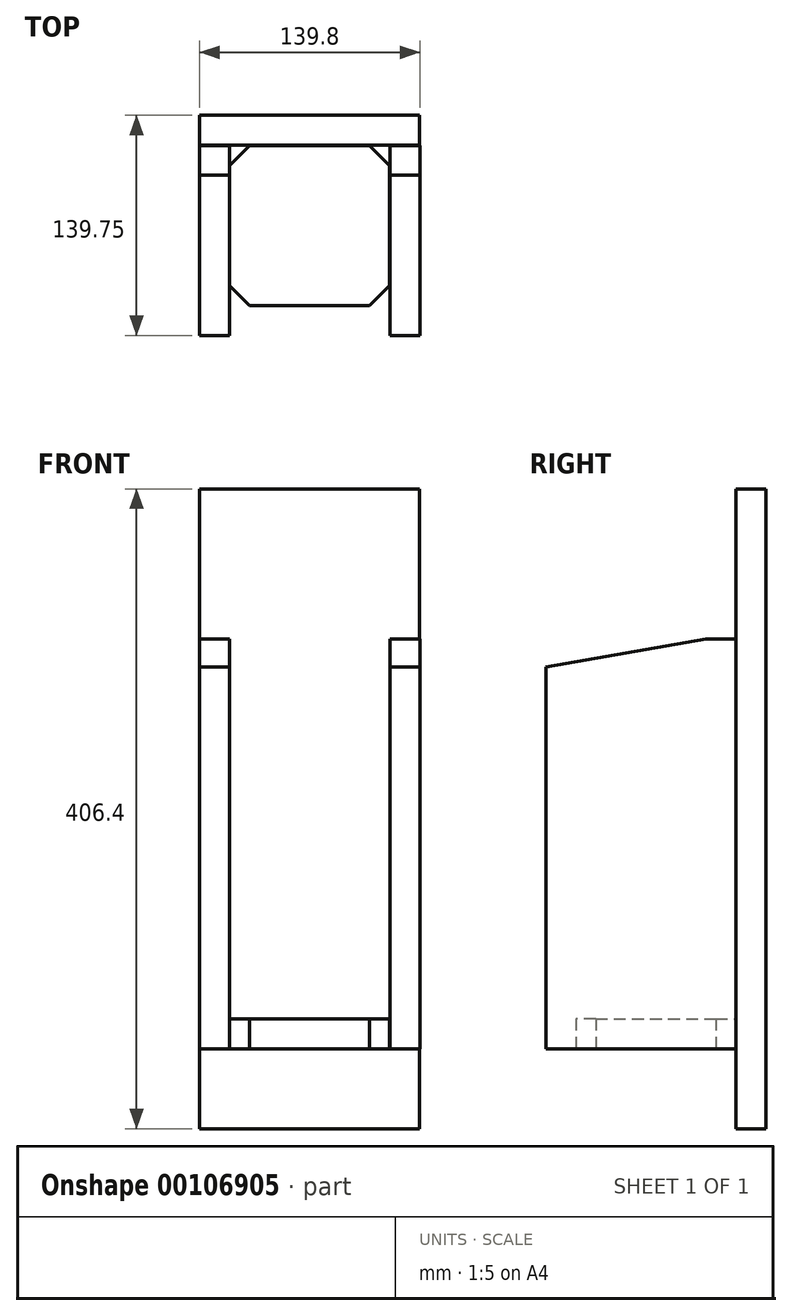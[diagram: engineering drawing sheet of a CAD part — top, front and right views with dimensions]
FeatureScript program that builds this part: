
annotation { "Feature Type Name" : "Feature", "Feature Type Description" : "" }
export const myFeature = defineFeature(function(context is Context, id is Id, definition is map)
    precondition{}
    {
        {
            var Q0;
            Q0=qCreatedBy(makeId("Top.planeOp"),FACE);
            var sketch = newSketch(context, id + "F0", { "sketchPlane" : qUnion([Q0])});
            skLineSegment(sketch, "E0.bottom", {"start": v(38.1, -50.8) * mm, "end": v(-38.1, -50.8) * mm});
            skLineSegment(sketch, "E0.top", {"start": v(38.1, 50.8) * mm, "end": v(-38.1, 50.8) * mm});
            skLineSegment(sketch, "E0.left", {"start": v(50.8, -38.1) * mm, "end": v(50.8, 38.1) * mm});
            skLineSegment(sketch, "E0.right", {"start": v(-50.8, -38.1) * mm, "end": v(-50.8, 38.1) * mm});
            skPoint(sketch, "E0.middle", {"position": v(0, 0) * mm});
            skLineSegment(sketch, "E1", {"start": v(-50.8, 38.1) * mm, "end": v(-38.1, 50.8) * mm});
            skPoint(sketch, "E2.orphan", {"position": v(-50.8, 50.8) * mm});
            skLineSegment(sketch, "E3", {"start": v(38.1, 50.8) * mm, "end": v(50.8, 38.1) * mm});
            skLineSegment(sketch, "E4", {"start": v(-50.8, -38.1) * mm, "end": v(-38.1, -50.8) * mm});
            skLineSegment(sketch, "E5", {"start": v(38.1, -50.8) * mm, "end": v(50.8, -38.1) * mm});
            skPoint(sketch, "E6.orphan", {"position": v(50.8, 50.8) * mm});
            skPoint(sketch, "E7.orphan", {"position": v(50.8, -50.8) * mm});
            skPoint(sketch, "E8.orphan", {"position": v(-50.8, -50.8) * mm});
            skSolve(sketch);
        }
        {
            var Q0;
            Q0=makeQuery(id+"F0.imprint","IMPRINT",FACE,{"disambiguationData":[TD([[makeQuery(id+"F0.imprint","IMPRINT",EDGE,{"derivedFrom":sQuery(id+"F0.wireOp",EDGE,"E0.bottom")}),-1.0]])]});
            extrude(context, id + "F1", {"entities" : qUnion([Q0]), "depth" : 19.05 * mm});
        }
        {
            var Q0;
            Q0=qCreatedBy(makeId("Top.planeOp"),FACE);
            var sketch = newSketch(context, id + "F2", { "sketchPlane" : qUnion([Q0])});
            skLineSegment(sketch, "E9.bottom", {"start": v(-69.85, 50.85) * mm, "end": v(69.85, 50.85) * mm});
            skLineSegment(sketch, "E9.top", {"start": v(-69.85, 69.9) * mm, "end": v(69.85, 69.9) * mm});
            skLineSegment(sketch, "E9.left", {"start": v(-69.85, 50.85) * mm, "end": v(-69.85, 69.9) * mm});
            skLineSegment(sketch, "E9.right", {"start": v(69.85, 50.85) * mm, "end": v(69.85, 69.9) * mm});
            skSolve(sketch);
        }
        {
            var Q0;
            Q0=makeQuery(id+"F2.imprint","IMPRINT",FACE,{"disambiguationData":[TD([[makeQuery(id+"F2.imprint","IMPRINT",EDGE,{"derivedFrom":sQuery(id+"F2.wireOp",EDGE,"E9.bottom")}),1.0]])]});
            extrude(context, id + "F3", {"entities" : qUnion([Q0]), "depth" : 355.6 * mm, "hasSecondDirection" : true, "secondDirectionOppositeDirection" : true, "secondDirectionDepth" : 50.8 * mm});
        }
        {
            var Q0;
            Q0=qCreatedBy(makeId("Top.planeOp"),FACE);
            var sketch = newSketch(context, id + "F4", { "sketchPlane" : qUnion([Q0])});
            skLineSegment(sketch, "E10.bottom", {"start": v(50.85, 50.8) * mm, "end": v(69.9, 50.8) * mm});
            skLineSegment(sketch, "E10.top", {"start": v(50.85, -69.85) * mm, "end": v(69.9, -69.85) * mm});
            skLineSegment(sketch, "E10.left", {"start": v(50.85, 50.8) * mm, "end": v(50.85, -69.85) * mm});
            skLineSegment(sketch, "E10.right", {"start": v(69.9, 50.8) * mm, "end": v(69.9, -69.85) * mm});
            skSolve(sketch);
        }
        {
            var Q0;
            Q0=makeQuery(id+"F4.imprint","IMPRINT",FACE,{"disambiguationData":[TD([[makeQuery(id+"F4.imprint","IMPRINT",EDGE,{"derivedFrom":sQuery(id+"F4.wireOp",EDGE,"E10.bottom")}),-1.0]])]});
            extrude(context, id + "F5", {"entities" : qUnion([Q0]), "depth" : 260.35 * mm});
        }
        {
            var Q0;
            Q0=makeQuery(id+"F5.opExtrude","SWEPT_FACE",FACE,{"disambiguationData":[OSD([sQuery(id+"F4.wireOp",EDGE,"E10.right")])]});
            var sketch = newSketch(context, id + "F6", { "sketchPlane" : qUnion([Q0])});
            skLineSegment(sketch, "E11", {"start": v(-69.85, 260.35) * mm, "end": v(-69.85, 242.43) * mm});
            skLineSegment(sketch, "E12", {"start": v(-69.85, 242.43) * mm, "end": v(31.8, 260.35) * mm});
            skLineSegment(sketch, "E13", {"start": v(31.8, 260.35) * mm, "end": v(-69.85, 260.35) * mm});
            skSolve(sketch);
        }
        {
            var Q0;
            Q0=makeQuery(id+"F6.imprint","IMPRINT",FACE,{"disambiguationData":[TD([[makeQuery(id+"F6.imprint","IMPRINT",EDGE,{"derivedFrom":sQuery(id+"F6.wireOp",EDGE,"E11")}),1.0]])]});
            extrude(context, id + "F7", {"entities" : qUnion([Q0]), "operationType" : NewBodyOperationType.REMOVE, "endBound" : BoundingType.THROUGH_ALL, "oppositeDirection" : true, "depth" : 25.4 * mm});
        }
        {
            var Q0;
            Q0=makeQuery(id+"F5.opExtrude","SWEPT_BODY",BODY,{"disambiguationData":[OSD([sQuery(id+"F4.wireOp",EDGE,"E10.bottom"),sQuery(id+"F4.wireOp",EDGE,"E10.top"),sQuery(id+"F4.wireOp",EDGE,"E10.left"),sQuery(id+"F4.wireOp",EDGE,"E10.right")])]});
            var Q1;
            Q1=qCreatedBy(makeId("Right.planeOp"),FACE);
            mirror(context, id + "F8", {"entities" : qUnion([Q0]), "mirrorPlane" : qUnion([Q1])});
        }
    });
